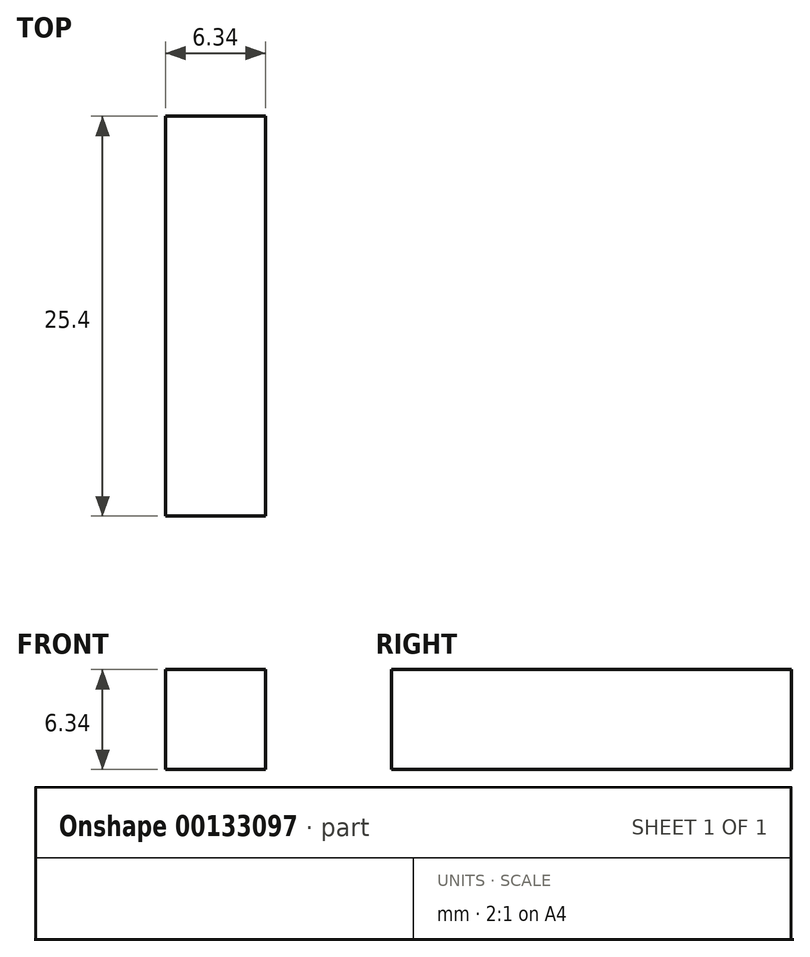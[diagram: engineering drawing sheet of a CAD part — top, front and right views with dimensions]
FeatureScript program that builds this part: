
annotation { "Feature Type Name" : "Feature", "Feature Type Description" : "" }
export const myFeature = defineFeature(function(context is Context, id is Id, definition is map)
    precondition{}
    {
        {
            var Q0;
            Q0=qCreatedBy(makeId("Front.planeOp"),FACE);
            var sketch = newSketch(context, id + "F0", { "sketchPlane" : qUnion([Q0])});
            skLineSegment(sketch, "E0.bottom", {"start": v(3.18, 3.18) * mm, "end": v(-3.17, 3.18) * mm});
            skLineSegment(sketch, "E0.top", {"start": v(3.17, -3.18) * mm, "end": v(-3.17, -3.18) * mm});
            skLineSegment(sketch, "E0.left", {"start": v(3.18, 3.18) * mm, "end": v(3.17, -3.17) * mm});
            skLineSegment(sketch, "E0.right", {"start": v(-3.17, 3.18) * mm, "end": v(-3.18, -3.17) * mm});
            skPoint(sketch, "E0.middle", {"position": v(0, 0) * mm});
            skSolve(sketch);
        }
        {
            var Q0;
            Q0 = qSketchRegion(id + "F0", true);
            extrude(context, id + "F1", {"entities" : qUnion([Q0]), "depth" : 25.4 * mm});
        }
    });
